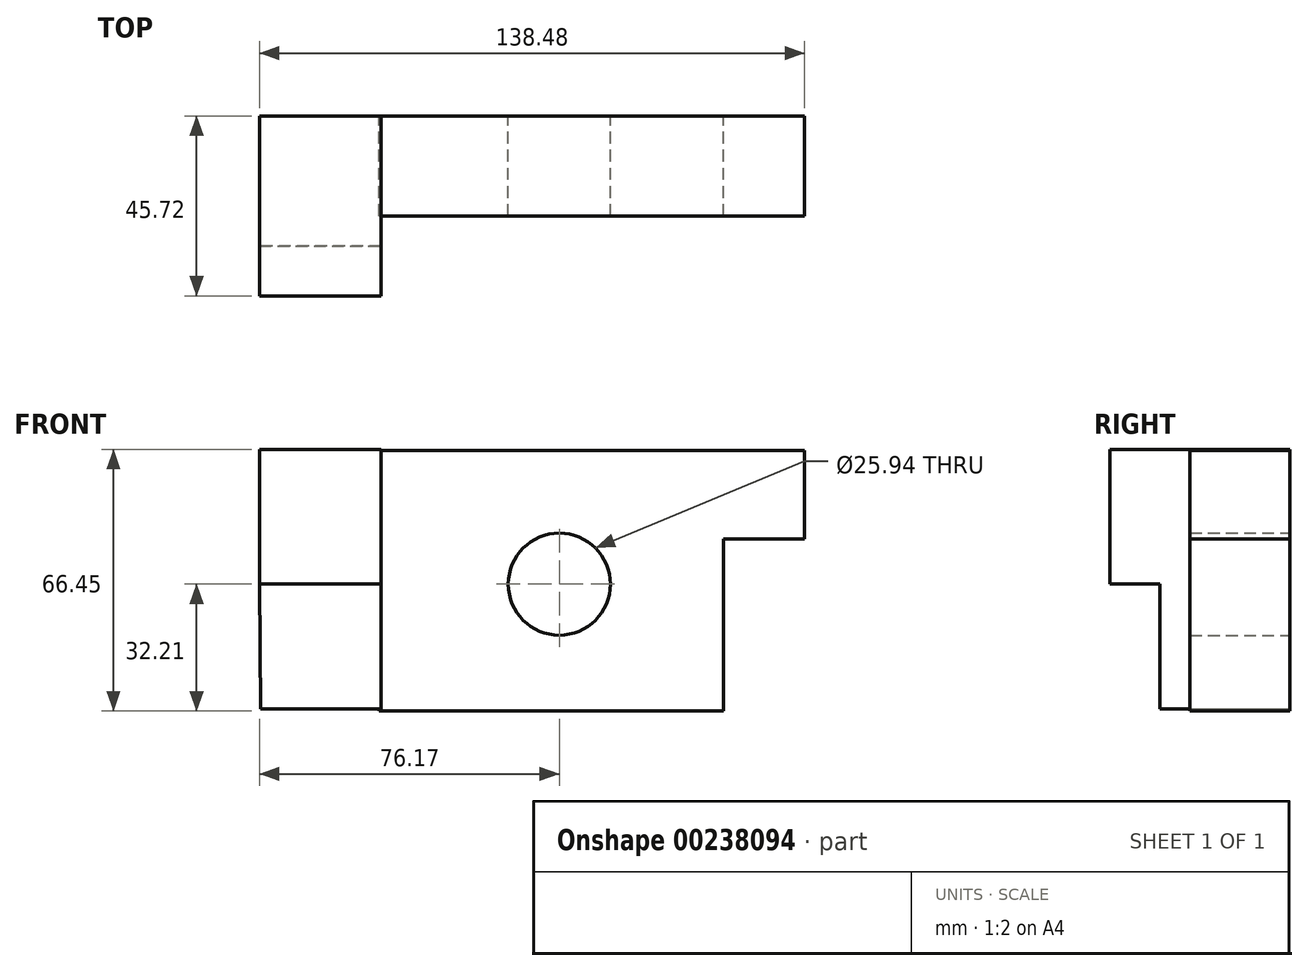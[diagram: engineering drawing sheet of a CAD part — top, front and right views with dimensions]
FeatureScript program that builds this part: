
annotation { "Feature Type Name" : "Feature", "Feature Type Description" : "" }
export const myFeature = defineFeature(function(context is Context, id is Id, definition is map)
    precondition{}
    {
        {
            var Q0;
            Q0=qCreatedBy(makeId("Front.planeOp"),FACE);
            var sketch = newSketch(context, id + "F0", { "sketchPlane" : qUnion([Q0])});
            skCircle(sketch, "E0", {"center": v(0, 0) * mm, "radius": 12.97 * mm});
            skLineSegment(sketch, "E1", {"start": v(0, -32.2) * mm, "end": v(-45.76, -32.2) * mm});
            skLineSegment(sketch, "E2", {"start": v(-45.76, -32.2) * mm, "end": v(-45.76, 33.96) * mm});
            skLineSegment(sketch, "E3", {"start": v(0, -32.2) * mm, "end": v(41.68, -32.2) * mm});
            skLineSegment(sketch, "E4", {"start": v(62.3, 33.96) * mm, "end": v(-45.76, 33.96) * mm});
            skLineSegment(sketch, "E5", {"start": v(41.68, -32.2) * mm, "end": v(41.68, 11.51) * mm});
            skLineSegment(sketch, "E6", {"start": v(62.3, 33.96) * mm, "end": v(62.3, 11.51) * mm});
            skLineSegment(sketch, "E7", {"start": v(62.3, 11.51) * mm, "end": v(41.68, 11.51) * mm});
            skSolve(sketch);
        }
        {
            var Q0;
            Q0=qCreatedBy(makeId("Front.planeOp"),FACE);
            var sketch = newSketch(context, id + "F1", { "sketchPlane" : qUnion([Q0])});
            skLineSegment(sketch, "E8", {"start": v(-45.23, 0) * mm, "end": v(-76.17, 0) * mm});
            skLineSegment(sketch, "E9", {"start": v(-45.23, 0) * mm, "end": v(-45.23, 34.24) * mm});
            skLineSegment(sketch, "E10", {"start": v(-76.17, 0) * mm, "end": v(-76.17, 34.24) * mm});
            skLineSegment(sketch, "E11", {"start": v(-45.23, 34.24) * mm, "end": v(-76.17, 34.24) * mm});
            skSolve(sketch);
        }
        {
            var Q0;
            Q0=qCreatedBy(makeId("Front.planeOp"),FACE);
            var sketch = newSketch(context, id + "F2", { "sketchPlane" : qUnion([Q0])});
            skLineSegment(sketch, "E12", {"start": v(-182.52, 2673.53) * mm, "end": v(-211.15, 2673.53) * mm});
            skLineSegment(sketch, "E13", {"start": v(-76.17, 0) * mm, "end": v(-45.23, 0) * mm});
            skLineSegment(sketch, "E14", {"start": v(-45.23, 0) * mm, "end": v(-45.23, -31.63) * mm});
            skLineSegment(sketch, "E15", {"start": v(-45.23, -31.63) * mm, "end": v(-75.91, -31.63) * mm});
            skLineSegment(sketch, "E16", {"start": v(-75.91, -31.63) * mm, "end": v(-76.17, 0) * mm});
            skSolve(sketch);
        }
        {
            var Q0;
            Q0 = qSketchRegion(id + "F2", true);
            extrude(context, id + "F3", {"entities" : qUnion([Q0]), "depth" : 33.02 * mm});
        }
        {
            var Q0;
            Q0 = qSketchRegion(id + "F1", true);
            extrude(context, id + "F4", {"entities" : qUnion([Q0]), "operationType" : NewBodyOperationType.ADD, "depth" : 45.72 * mm});
        }
        {
            var Q0;
            Q0 = qSketchRegion(id + "F0", true);
            extrude(context, id + "F5", {"entities" : qUnion([Q0]), "operationType" : NewBodyOperationType.ADD, "depth" : 25.4 * mm});
        }
    });
